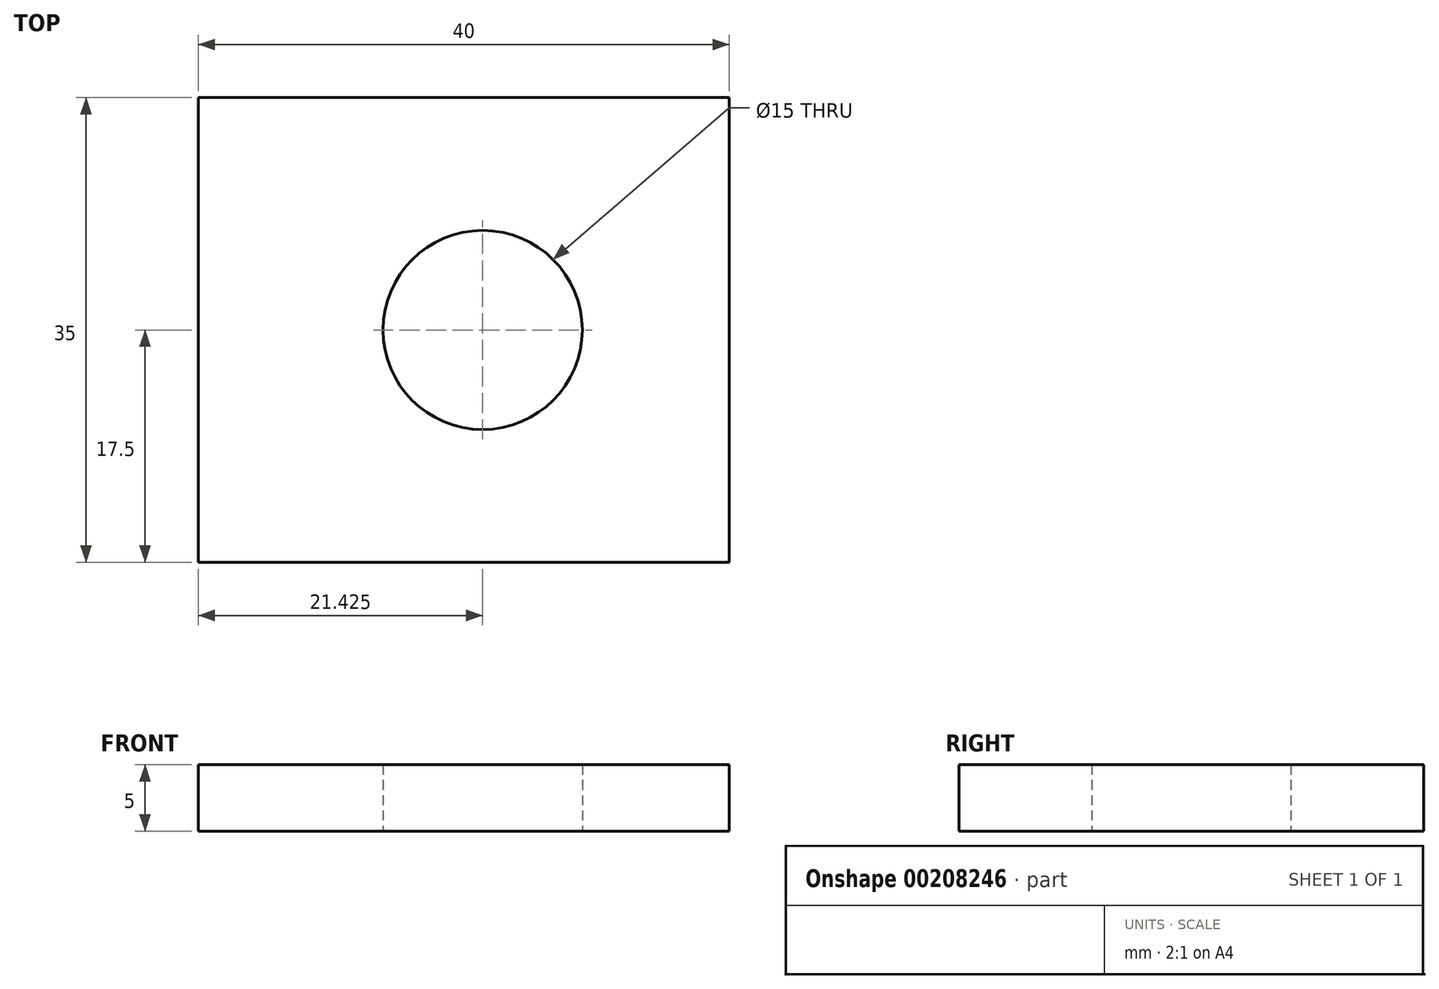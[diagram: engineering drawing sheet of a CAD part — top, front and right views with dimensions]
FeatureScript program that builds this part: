
annotation { "Feature Type Name" : "Feature", "Feature Type Description" : "" }
export const myFeature = defineFeature(function(context is Context, id is Id, definition is map)
    precondition{}
    {
        {
            var Q0;
            Q0=qCreatedBy(makeId("Top.planeOp"),FACE);
            var sketch = newSketch(context, id + "F0", { "sketchPlane" : qUnion([Q0])});
            skLineSegment(sketch, "E0.bottom", {"start": v(0, 0) * mm, "end": v(40, 0) * mm});
            skLineSegment(sketch, "E0.top", {"start": v(0, 35) * mm, "end": v(40, 35) * mm});
            skLineSegment(sketch, "E0.left", {"start": v(0, 0) * mm, "end": v(0, 35) * mm});
            skLineSegment(sketch, "E0.right", {"start": v(40, 0) * mm, "end": v(40, 35) * mm});
            skCircle(sketch, "E1", {"center": v(21.42, 17.5) * mm, "radius": 7.5 * mm});
            skSolve(sketch);
        }
        {
            var Q0;
            Q0=makeQuery(id+"F0.imprint","IMPRINT",FACE,{"disambiguationData":[TD([[makeQuery(id+"F0.imprint","IMPRINT",EDGE,{"derivedFrom":sQuery(id+"F0.wireOp",EDGE,"E0.bottom")}),1.0]])]});
            extrude(context, id + "F1", {"entities" : qUnion([Q0]), "depth" : 5 * mm});
        }
    });
